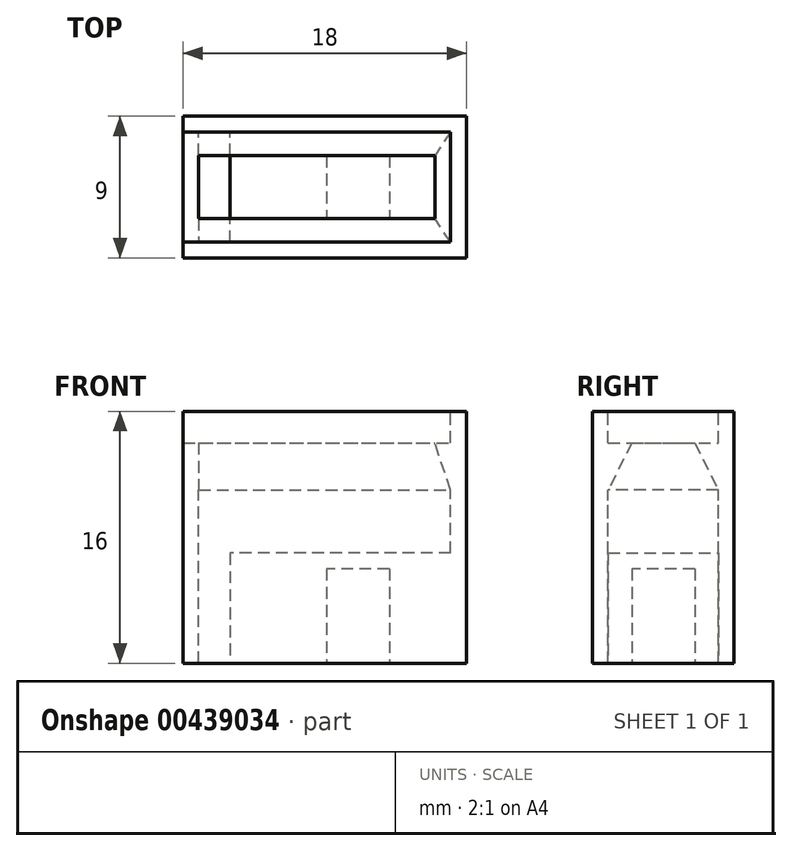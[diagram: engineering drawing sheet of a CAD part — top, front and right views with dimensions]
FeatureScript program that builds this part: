
annotation { "Feature Type Name" : "Feature", "Feature Type Description" : "" }
export const myFeature = defineFeature(function(context is Context, id is Id, definition is map)
    precondition{}
    {
        {
            var Q0;
            Q0=qCreatedBy(makeId("Top.planeOp"),FACE);
            var sketch = newSketch(context, id + "F0", { "sketchPlane" : qUnion([Q0])});
            skLineSegment(sketch, "E0.bottom", {"start": v(9, -4.5) * mm, "end": v(-9, -4.5) * mm});
            skLineSegment(sketch, "E0.top", {"start": v(9, 4.5) * mm, "end": v(-9, 4.5) * mm});
            skLineSegment(sketch, "E0.left", {"start": v(9, -4.5) * mm, "end": v(9, 4.5) * mm});
            skLineSegment(sketch, "E0.right", {"start": v(-9, -4.5) * mm, "end": v(-9, 4.5) * mm});
            skPoint(sketch, "E0.middle", {"position": v(0, 0) * mm});
            skSolve(sketch);
        }
        {
            var Q0;
            Q0=qSketchRegion(id+"F0",true);
            extrude(context, id + "F1", {"entities" : qUnion([Q0]), "depth" : 14 * mm});
        }
        {
            var Q0;
            Q0=makeQuery(id+"F1.opExtrude","CAP_FACE",FACE,{"disambiguationData":[OSD([sQuery(id+"F0.wireOp",EDGE,"E0.bottom"),sQuery(id+"F0.wireOp",EDGE,"E0.top"),sQuery(id+"F0.wireOp",EDGE,"E0.left"),sQuery(id+"F0.wireOp",EDGE,"E0.right")])],"isStart":false});
            var sketch = newSketch(context, id + "F2", { "sketchPlane" : qUnion([Q0])});
            skLineSegment(sketch, "E1.bottom", {"start": v(8, -3.5) * mm, "end": v(-8, -3.5) * mm});
            skLineSegment(sketch, "E1.top", {"start": v(8, 3.5) * mm, "end": v(-8, 3.5) * mm});
            skLineSegment(sketch, "E1.left", {"start": v(8, -3.5) * mm, "end": v(8, 3.5) * mm});
            skLineSegment(sketch, "E1.right", {"start": v(-8, -3.5) * mm, "end": v(-8, 3.5) * mm});
            skPoint(sketch, "E1.middle", {"position": v(0, 0) * mm});
            skSolve(sketch);
        }
        {
            var Q0;
            Q0=qSketchRegion(id+"F2",true);
            extrude(context, id + "F3", {"entities" : qUnion([Q0]), "operationType" : NewBodyOperationType.REMOVE, "oppositeDirection" : true, "depth" : 7 * mm});
        }
        {
            var Q0;
            Q0=makeQuery(id+"F1.opExtrude","CAP_FACE",FACE,{"disambiguationData":[OSD([sQuery(id+"F0.wireOp",EDGE,"E0.bottom"),sQuery(id+"F0.wireOp",EDGE,"E0.top"),sQuery(id+"F0.wireOp",EDGE,"E0.left"),sQuery(id+"F0.wireOp",EDGE,"E0.right")])],"isStart":true});
            var sketch = newSketch(context, id + "F4", { "sketchPlane" : qUnion([Q0])});
            skLineSegment(sketch, "E2.bottom", {"start": v(4.1, -2) * mm, "end": v(0.1, -2) * mm});
            skLineSegment(sketch, "E2.top", {"start": v(4.1, 2) * mm, "end": v(0.1, 2) * mm});
            skLineSegment(sketch, "E2.left", {"start": v(4.1, -2) * mm, "end": v(4.1, 2) * mm});
            skLineSegment(sketch, "E2.right", {"start": v(0.1, -2) * mm, "end": v(0.1, 2) * mm});
            skPoint(sketch, "E2.middle", {"position": v(2.1, 0) * mm});
            skLineSegment(sketch, "E3.bottom", {"start": v(-6, -3.5) * mm, "end": v(-8, -3.5) * mm});
            skLineSegment(sketch, "E3.top", {"start": v(-6, 3.5) * mm, "end": v(-8, 3.5) * mm});
            skLineSegment(sketch, "E3.left", {"start": v(-6, -3.5) * mm, "end": v(-6, 3.5) * mm});
            skLineSegment(sketch, "E3.right", {"start": v(-8, -3.5) * mm, "end": v(-8, 3.5) * mm});
            skPoint(sketch, "E3.middle", {"position": v(-7, 0) * mm});
            skSolve(sketch);
        }
        {
            var Q0;
            Q0=makeQuery(id+"F4.imprint","IMPRINT",FACE,{"disambiguationData":[TD([[makeQuery(id+"F4.imprint","IMPRINT",EDGE,{"derivedFrom":sQuery(id+"F4.wireOp",EDGE,"E2.bottom")}),-1.0]])]});
            extrude(context, id + "F5", {"entities" : qUnion([Q0]), "operationType" : NewBodyOperationType.REMOVE, "oppositeDirection" : true, "depth" : 6 * mm});
        }
        {
            var Q0;
            Q0=makeQuery(id+"F4.imprint","IMPRINT",FACE,{"disambiguationData":[TD([[makeQuery(id+"F4.imprint","IMPRINT",EDGE,{"derivedFrom":sQuery(id+"F4.wireOp",EDGE,"E3.bottom")}),-1.0]])]});
            extrude(context, id + "F6", {"entities" : qUnion([Q0]), "operationType" : NewBodyOperationType.REMOVE, "oppositeDirection" : true, "depth" : 9 * mm});
        }
        {
            var Q0;
            Q0=makeQuery(id+"F1.opExtrude","CAP_FACE",FACE,{"disambiguationData":[OSD([sQuery(id+"F0.wireOp",EDGE,"E0.bottom"),sQuery(id+"F0.wireOp",EDGE,"E0.top"),sQuery(id+"F0.wireOp",EDGE,"E0.left"),sQuery(id+"F0.wireOp",EDGE,"E0.right")])],"isStart":false});
            var sketch = newSketch(context, id + "F7", { "sketchPlane" : qUnion([Q0])});
            skLineSegment(sketch, "E4", {"start": v(-9, 4.5) * mm, "end": v(9, 4.5) * mm});
            skLineSegment(sketch, "E5", {"start": v(9, 4.5) * mm, "end": v(9, -4.5) * mm});
            skLineSegment(sketch, "E6", {"start": v(9, -4.5) * mm, "end": v(-9, -4.5) * mm});
            skLineSegment(sketch, "E7", {"start": v(-9, -4.5) * mm, "end": v(-9, -3.5) * mm});
            skLineSegment(sketch, "E8", {"start": v(-9, -3.5) * mm, "end": v(8, -3.5) * mm});
            skLineSegment(sketch, "E9", {"start": v(8, -3.5) * mm, "end": v(8, 3.5) * mm});
            skLineSegment(sketch, "E10", {"start": v(8, 3.5) * mm, "end": v(-9, 3.5) * mm});
            skLineSegment(sketch, "E11", {"start": v(-9, 3.5) * mm, "end": v(-9, 4.5) * mm});
            skSolve(sketch);
        }
        {
            var Q0;
            Q0=qSketchRegion(id+"F7",true);
            extrude(context, id + "F8", {"entities" : qUnion([Q0]), "operationType" : NewBodyOperationType.ADD, "depth" : 2 * mm});
        }
        {
            var Q0;
            Q0=makeQuery(id+"F8.boolean.opBoolean","MERGE",FACE,{"derivedFrom":[makeQuery(id+"F6.boolean.opBoolean","MERGE",FACE,{"derivedFrom":[makeQuery(id+"F3.boolean.opBoolean","COPY",FACE,{"derivedFrom":makeQuery(id+"F3.opExtrude","SWEPT_FACE",FACE,{"disambiguationData":[OSD([sQuery(id+"F2.wireOp",EDGE,"E1.bottom")])]})}),makeQuery(id+"F6.opExtrude","SWEPT_FACE",FACE,{"disambiguationData":[OSD([sQuery(id+"F4.wireOp",EDGE,"E3.top")])]})]}),makeQuery(id+"F8.opExtrude","SWEPT_FACE",FACE,{"disambiguationData":[OSD([sQuery(id+"F7.wireOp",EDGE,"E8")])]})]});
            var sketch = newSketch(context, id + "F9", { "sketchPlane" : qUnion([Q0])});
            skLineSegment(sketch, "E12", {"start": v(-8, 14) * mm, "end": v(-7, 14) * mm});
            skLineSegment(sketch, "E13", {"start": v(8, 14) * mm, "end": v(6.5, 14) * mm, "construction": true});
            skLineSegment(sketch, "E14", {"start": v(6.5, 14) * mm, "end": v(8, 7) * mm, "construction": true});
            skLineSegment(sketch, "E15", {"start": v(8, 7) * mm, "end": v(8, 14) * mm, "construction": true});
            skLineSegment(sketch, "E16", {"start": v(-7, 14) * mm, "end": v(-8, 11) * mm});
            skLineSegment(sketch, "E17", {"start": v(-8, 11) * mm, "end": v(-8, 14) * mm});
            skSolve(sketch);
        }
        {
            var Q0;
            Q0=qSketchRegion(id+"F9",true);
            extrude(context, id + "F10", {"entities" : qUnion([Q0]), "depth" : 7 * mm});
        }
        {
            var Q0;
            Q0=makeQuery(id+"F8.boolean.opBoolean","MERGE",FACE,{"derivedFrom":[makeQuery(id+"F3.boolean.opBoolean","COPY",FACE,{"derivedFrom":makeQuery(id+"F3.opExtrude","SWEPT_FACE",FACE,{"disambiguationData":[OSD([sQuery(id+"F2.wireOp",EDGE,"E1.left")])]})}),makeQuery(id+"F8.opExtrude","SWEPT_FACE",FACE,{"disambiguationData":[OSD([sQuery(id+"F7.wireOp",EDGE,"E9")])]})]});
            var sketch = newSketch(context, id + "F11", { "sketchPlane" : qUnion([Q0])});
            skLineSegment(sketch, "E18", {"start": v(3.5, 14) * mm, "end": v(2, 14) * mm});
            skLineSegment(sketch, "E19", {"start": v(-2, 14) * mm, "end": v(-3.5, 14) * mm});
            skLineSegment(sketch, "E20", {"start": v(2, 14) * mm, "end": v(3.5, 11) * mm});
            skLineSegment(sketch, "E21", {"start": v(3.5, 11) * mm, "end": v(3.5, 14) * mm});
            skLineSegment(sketch, "E22", {"start": v(-2, 14) * mm, "end": v(-3.5, 11) * mm});
            skLineSegment(sketch, "E23", {"start": v(-3.5, 11) * mm, "end": v(-3.5, 14) * mm});
            skSolve(sketch);
        }
        {
            var Q0;
            Q0=qSketchRegion(id+"F11",true);
            extrude(context, id + "F12", {"entities" : qUnion([Q0]), "operationType" : NewBodyOperationType.ADD, "depth" : 16 * mm});
        }
    });
